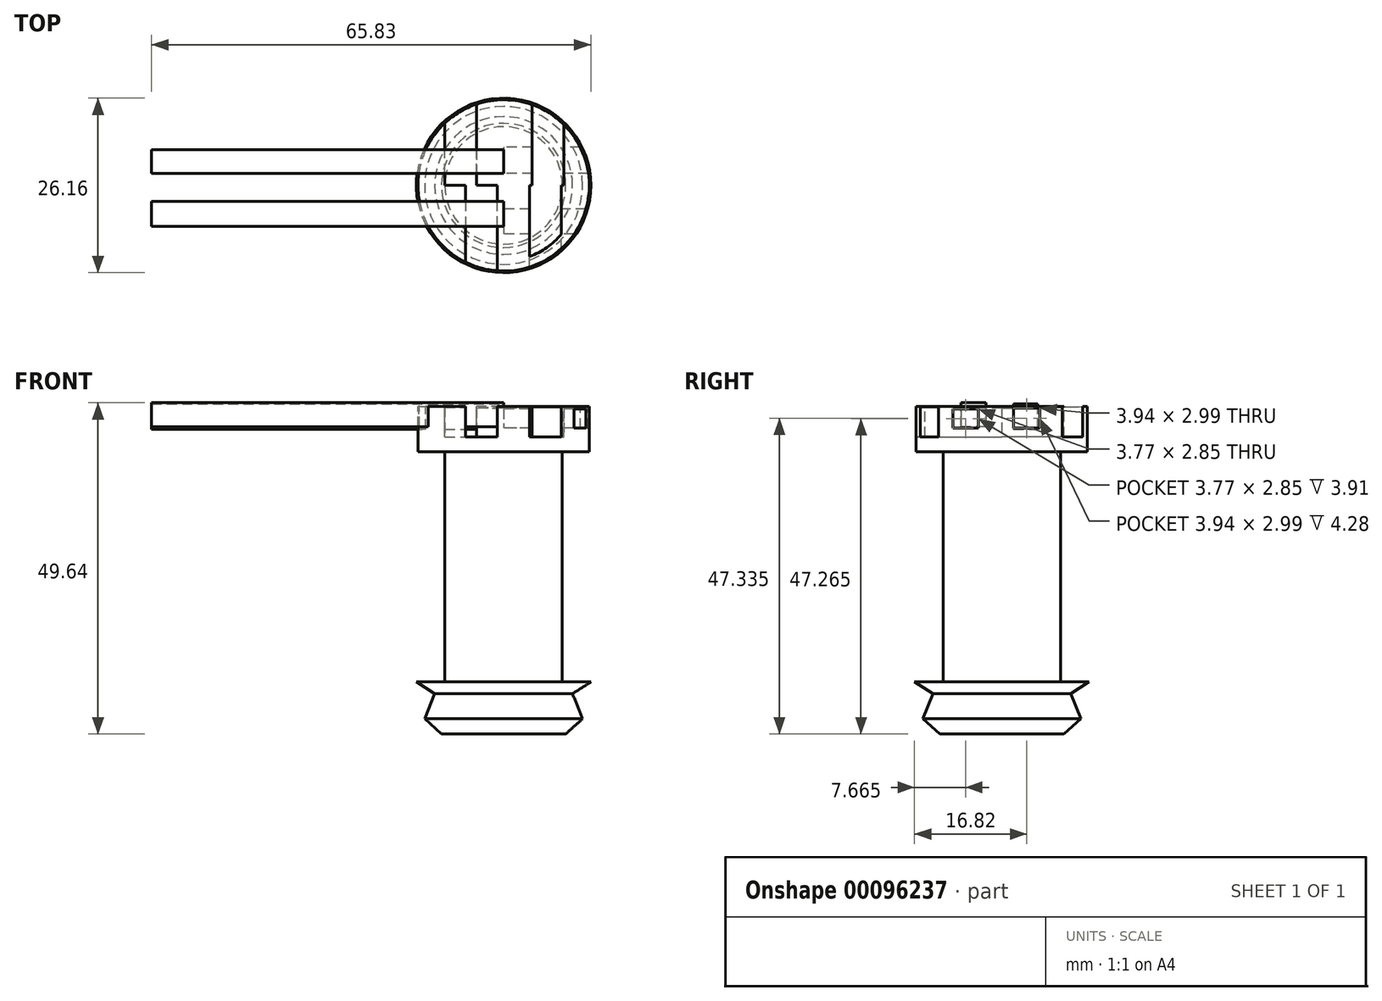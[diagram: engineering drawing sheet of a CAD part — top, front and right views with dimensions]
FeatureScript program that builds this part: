
annotation { "Feature Type Name" : "Feature", "Feature Type Description" : "" }
export const myFeature = defineFeature(function(context is Context, id is Id, definition is map)
    precondition{}
    {
        {
            var Q0;
            Q0=qCreatedBy(makeId("Front.planeOp"),FACE);
            var sketch = newSketch(context, id + "F0", { "sketchPlane" : qUnion([Q0])});
            skLineSegment(sketch, "E0", {"start": v(0, -42.27) * mm, "end": v(9.3, -42.27) * mm});
            skLineSegment(sketch, "E1", {"start": v(9.3, -42.27) * mm, "end": v(11.83, -40) * mm});
            skLineSegment(sketch, "E2", {"start": v(11.83, -40) * mm, "end": v(10.32, -36.23) * mm});
            skLineSegment(sketch, "E3", {"start": v(10.32, -36.23) * mm, "end": v(13.08, -34.47) * mm});
            skLineSegment(sketch, "E4", {"start": v(13.08, -34.47) * mm, "end": v(8.8, -34.47) * mm});
            skLineSegment(sketch, "E5", {"start": v(8.8, -34.47) * mm, "end": v(8.8, -22.9) * mm});
            skLineSegment(sketch, "E6", {"start": v(8.8, -22.9) * mm, "end": v(8.8, -8.05) * mm});
            skLineSegment(sketch, "E7", {"start": v(8.8, -8.05) * mm, "end": v(8.8, 0) * mm});
            skLineSegment(sketch, "E8", {"start": v(8.8, 0) * mm, "end": v(12.83, 0) * mm});
            skLineSegment(sketch, "E9", {"start": v(12.83, 0) * mm, "end": v(12.83, 6.8) * mm});
            skLineSegment(sketch, "E10", {"start": v(12.83, 6.8) * mm, "end": v(0, 6.54) * mm});
            skLineSegment(sketch, "E11", {"start": v(0, 6.54) * mm, "end": v(0, -42.27) * mm});
            skSolve(sketch);
        }
        {
            var Q0;
            Q0 = qSketchRegion(id + "F0", true);
            var Q1;
            Q1=makeQuery(id+"F0.imprint","IMPRINT",FACE,{"disambiguationData":[TD([[makeQuery(id+"F0.imprint","IMPRINT",EDGE,{"derivedFrom":sQuery(id+"F0.wireOp",EDGE,"E0")}),1.0]])]});
            var Q2;
            Q2=sQuery(id+"F0.wireOp",EDGE,"E11");
            revolve(context, id + "F1", {"entities" : qUnion([Q0, Q1]), "axis" : qUnion([Q2]), "revolveType" : RevolveType.FULL});
        }
        {
            var Q0;
            Q0=qCreatedBy(makeId("Front.planeOp"),FACE);
            var sketch = newSketch(context, id + "F2", { "sketchPlane" : qUnion([Q0])});
            skLineSegment(sketch, "E12.bottom", {"start": v(-8.8, 7.04) * mm, "end": v(-4.03, 7.04) * mm});
            skLineSegment(sketch, "E12.top", {"start": v(-8.8, 2.26) * mm, "end": v(-4.03, 2.26) * mm});
            skLineSegment(sketch, "E12.left", {"start": v(-8.8, 7.04) * mm, "end": v(-8.8, 2.26) * mm});
            skLineSegment(sketch, "E12.right", {"start": v(-4.03, 7.04) * mm, "end": v(-4.03, 2.26) * mm});
            skLineSegment(sketch, "E13.bottom", {"start": v(4.28, 7.04) * mm, "end": v(9.06, 7.04) * mm});
            skLineSegment(sketch, "E13.top", {"start": v(4.28, 2.26) * mm, "end": v(9.06, 2.26) * mm});
            skLineSegment(sketch, "E13.left", {"start": v(4.28, 7.04) * mm, "end": v(4.28, 2.26) * mm});
            skLineSegment(sketch, "E13.right", {"start": v(9.06, 7.04) * mm, "end": v(9.06, 2.26) * mm});
            skSolve(sketch);
        }
        {
            var Q0;
            Q0 = qSketchRegion(id + "F2", true);
            extrude(context, id + "F3", {"entities" : qUnion([Q0]), "operationType" : NewBodyOperationType.REMOVE, "oppositeDirection" : true, "depth" : 25.4 * mm});
        }
        {
            var Q0;
            Q0=qCreatedBy(makeId("Front.planeOp"),FACE);
            var sketch = newSketch(context, id + "F4", { "sketchPlane" : qUnion([Q0])});
            skLineSegment(sketch, "E14.bottom", {"start": v(-5.7, 7.01) * mm, "end": v(-0.96, 7.01) * mm});
            skLineSegment(sketch, "E14.top", {"start": v(-5.7, 2.26) * mm, "end": v(-0.96, 2.26) * mm});
            skLineSegment(sketch, "E14.left", {"start": v(-5.7, 7.01) * mm, "end": v(-5.7, 2.26) * mm});
            skLineSegment(sketch, "E14.right", {"start": v(-0.96, 7.01) * mm, "end": v(-0.96, 2.26) * mm});
            skLineSegment(sketch, "E15.bottom", {"start": v(3.91, 6.77) * mm, "end": v(8.66, 6.77) * mm});
            skLineSegment(sketch, "E15.top", {"start": v(3.91, 2.26) * mm, "end": v(8.66, 2.26) * mm});
            skLineSegment(sketch, "E15.left", {"start": v(3.91, 6.77) * mm, "end": v(3.91, 2.26) * mm});
            skLineSegment(sketch, "E15.right", {"start": v(8.66, 6.77) * mm, "end": v(8.66, 2.26) * mm});
            skSolve(sketch);
        }
        {
            var Q0;
            Q0 = qSketchRegion(id + "F4", true);
            extrude(context, id + "F5", {"entities" : qUnion([Q0]), "operationType" : NewBodyOperationType.REMOVE, "depth" : 24.3 * mm});
        }
        {
            var Q0;
            Q0=qCreatedBy(makeId("Right.planeOp"),FACE);
            var sketch = newSketch(context, id + "F6", { "sketchPlane" : qUnion([Q0])});
            skLineSegment(sketch, "E16.bottom", {"start": v(5.71, 6.56) * mm, "end": v(1.77, 6.56) * mm});
            skLineSegment(sketch, "E16.top", {"start": v(5.71, 3.57) * mm, "end": v(1.77, 3.57) * mm});
            skLineSegment(sketch, "E16.left", {"start": v(5.71, 6.56) * mm, "end": v(5.71, 3.57) * mm});
            skLineSegment(sketch, "E16.right", {"start": v(1.77, 6.56) * mm, "end": v(1.77, 3.57) * mm});
            skLineSegment(sketch, "E17.bottom", {"start": v(-3.53, 6.42) * mm, "end": v(-7.3, 6.42) * mm});
            skLineSegment(sketch, "E17.top", {"start": v(-3.53, 3.57) * mm, "end": v(-7.3, 3.57) * mm});
            skLineSegment(sketch, "E17.left", {"start": v(-3.53, 6.42) * mm, "end": v(-3.53, 3.57) * mm});
            skLineSegment(sketch, "E17.right", {"start": v(-7.3, 6.42) * mm, "end": v(-7.3, 3.57) * mm});
            skSolve(sketch);
        }
        {
            var Q0;
            Q0 = qSketchRegion(id + "F6", true);
            extrude(context, id + "F7", {"entities" : qUnion([Q0]), "operationType" : NewBodyOperationType.REMOVE, "depth" : 27.23 * mm});
        }
        {
            var Q0;
            Q0=qCreatedBy(makeId("Right.planeOp"),FACE);
            var sketch = newSketch(context, id + "F8", { "sketchPlane" : qUnion([Q0])});
            skLineSegment(sketch, "E18.bottom", {"start": v(5.36, 7.18) * mm, "end": v(1.78, 7.18) * mm});
            skLineSegment(sketch, "E18.top", {"start": v(5.36, 3.41) * mm, "end": v(1.78, 3.41) * mm});
            skLineSegment(sketch, "E18.left", {"start": v(5.36, 7.18) * mm, "end": v(5.36, 3.41) * mm});
            skLineSegment(sketch, "E18.right", {"start": v(1.78, 7.18) * mm, "end": v(1.78, 3.41) * mm});
            skLineSegment(sketch, "E19.bottom", {"start": v(-2.37, 7.37) * mm, "end": v(-6.14, 7.37) * mm});
            skLineSegment(sketch, "E19.top", {"start": v(-2.37, 3.79) * mm, "end": v(-6.14, 3.79) * mm});
            skLineSegment(sketch, "E19.left", {"start": v(-2.37, 7.37) * mm, "end": v(-2.37, 3.79) * mm});
            skLineSegment(sketch, "E19.right", {"start": v(-6.14, 7.37) * mm, "end": v(-6.14, 3.79) * mm});
            skSolve(sketch);
        }
        {
            var Q0;
            Q0=makeQuery(id+"F8.imprint","IMPRINT",FACE,{"disambiguationData":[TD([[makeQuery(id+"F8.imprint","IMPRINT",EDGE,{"derivedFrom":sQuery(id+"F8.wireOp",EDGE,"E19.bottom")}),1.0]])]});
            var Q1;
            Q1=makeQuery(id+"F8.imprint","IMPRINT",FACE,{"disambiguationData":[TD([[makeQuery(id+"F8.imprint","IMPRINT",EDGE,{"derivedFrom":sQuery(id+"F8.wireOp",EDGE,"E18.bottom")}),1.0]])]});
            extrude(context, id + "F9", {"entities" : qUnion([Q0, Q1]), "operationType" : NewBodyOperationType.REMOVE, "oppositeDirection" : true, "depth" : 25.4 * mm});
        }
        {
            var Q0;
            Q0 = qSketchRegion(id + "F8", true);
            extrude(context, id + "F10", {"entities" : qUnion([Q0]), "operationType" : NewBodyOperationType.ADD, "oppositeDirection" : true, "depth" : 52.75 * mm});
        }
    });
